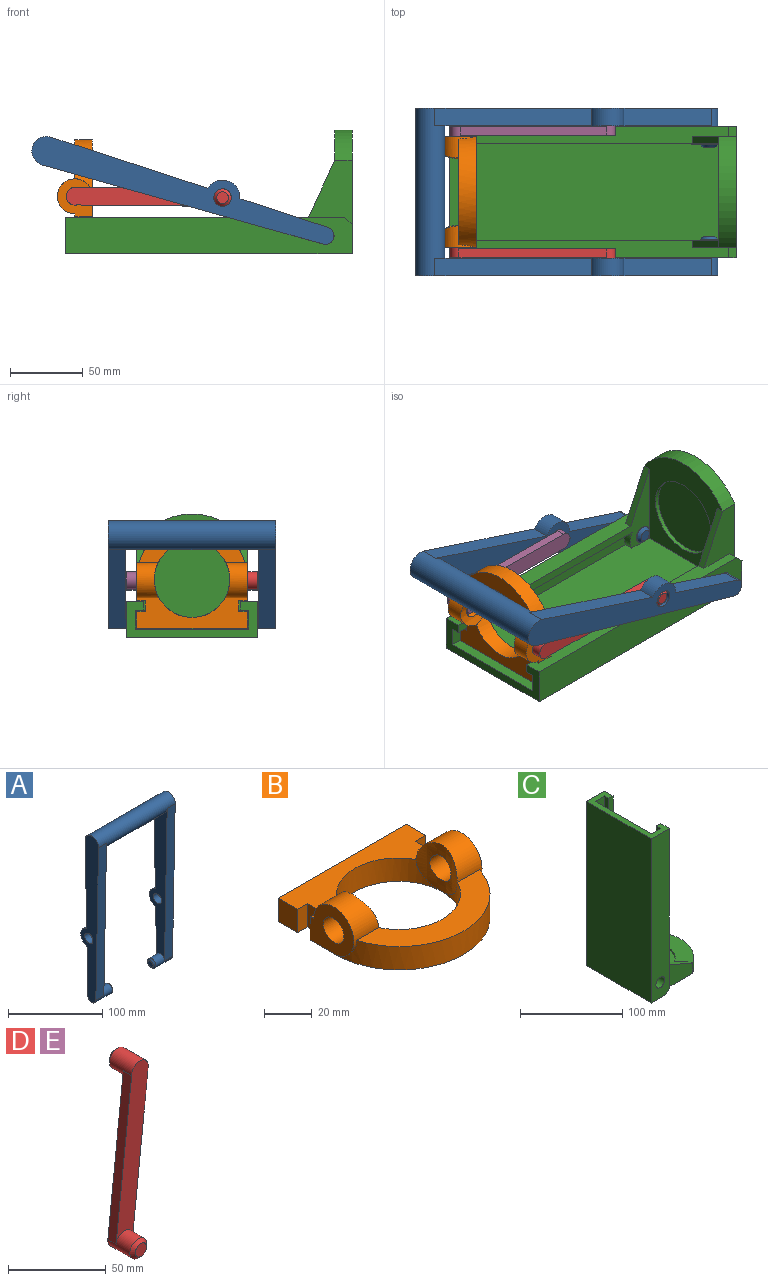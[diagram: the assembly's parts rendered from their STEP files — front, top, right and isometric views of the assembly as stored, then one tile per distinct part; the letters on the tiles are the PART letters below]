
ASSEMBLY  parts=5 mates=9
PART A: 21 faces, bbox 115x26.5x216 mm
  f0: plane 63.32x12mm, normal (0,1,-0.02), area 760mm2, adj f1,f6,f7,f8
  f1: cylinder r=6mm len=25mm, axis (-1,0,0), area 712.5mm2, adj f0,f3,f6,f7,f10
  f2: plane 8x8mm, normal (1,0,0), area 50.3mm2, adj f10
  f3: plane 200.12x12.01mm, normal (0,-1,-0.02), area 2401.9mm2, adj f1,f5,f6,f7
  f4: plane 113.24x12mm, normal (0,1,-0.02), area 1359.2mm2, adj f5,f6,f7,f8
  f5: cylinder r=10mm len=115mm, axis (1,0,0), area 6481.3mm2, adj f3,f4,f6,f7,f14,f15,f16,f17
  f6: plane 216x26.5mm, normal (-1,0,0), area 3451.9mm2, adj f0,f1,f3,f4,f5,f8,f9
  f7: plane 199.8x26.5mm, normal (1,0,0), area 3024.7mm2, adj f0,f1,f3,f4,f5,f8,f9
  f8: cylinder r=12mm len=23.23mm, axis (1,0,0), area 379.7mm2, adj f0,f4,f6,f7
  f9: cylinder r=6.1mm len=12.2mm, axis (-1,0,0), area 459.9mm2, adj f6,f7
  f10: cone r=4mm half-angle=45deg, axis (-1,0,0), area 88.9mm2, adj f1,f2
  f11: plane 63.32x12mm, normal (0,1,-0.02), area 760mm2, adj f12,f16,f17,f18
  f12: cylinder r=6mm len=25mm, axis (1,0,0), area 712.5mm2, adj f11,f14,f16,f17,f20
  f13: plane 8x8mm, normal (-1,0,0), area 50.3mm2, adj f20
  f14: plane 200.12x12.01mm, normal (0,-1,-0.02), area 2401.9mm2, adj f5,f12,f16,f17
  f15: plane 113.24x12mm, normal (0,1,-0.02), area 1359.2mm2, adj f5,f16,f17,f18
  f16: plane 216x26.5mm, normal (1,0,0), area 3451.9mm2, adj f5,f11,f12,f14,f15,f18,f19
  f17: plane 199.8x26.5mm, normal (-1,0,0), area 3024.7mm2, adj f5,f11,f12,f14,f15,f18,f19
  f18: cylinder r=12mm len=23.23mm, axis (-1,0,0), area 379.7mm2, adj f11,f15,f16,f17
  f19: cylinder r=6.1mm len=12.2mm, axis (1,0,0), area 459.9mm2, adj f16,f17
  f20: cone r=4mm half-angle=45deg, axis (1,0,0), area 88.9mm2, adj f12,f13
PART B: 23 faces, bbox 76x72x24 mm
  f0: extruded ~24x24mm, area 347.8mm2, adj f4,f5,f20,f22
  f1: extruded ~24x24mm, area 347.8mm2, adj f2,f4,f5,f21
  f2: cylinder r=12mm len=24mm, axis (-1,0,0), area 521.6mm2, adj f1,f3,f6,f7,f10
  f3: cylinder r=38mm len=76mm, axis (0,0,-1), area 1228.1mm2, adj f2,f7,f9,f10,f19,f20
  f4: cylinder r=26mm len=52mm, axis (0,0,-1), area 760.3mm2, adj f0,f1,f7,f19
  f5: cylinder r=26mm len=51.99mm, axis (0,0,-1), area 734.4mm2, adj f0,f1,f6,f19
  f6: plane 76x21mm, normal (0,0,1), area 1068.2mm2, adj f2,f5,f8,f9,f10,f11,f12,f13
  f7: plane 72.75x27mm, normal (0,0,1), area 960.1mm2, adj f2,f3,f4,f20
  f8: plane 12x6mm, normal (0,1,0), area 72mm2, adj f6,f9,f18,f19
  f9: plane 26x24mm, normal (-1,0,0), area 390.4mm2, adj f3,f6,f8,f19,f20,f22
  f10: plane 26x24mm, normal (1,0,0), area 390.4mm2, adj f2,f3,f6,f11,f19,f21
  f11: plane 12x6mm, normal (0,1,0), area 72mm2, adj f6,f10,f12,f19
  f12: plane 12x7.5mm, normal (1,0,0), area 90mm2, adj f6,f11,f13,f19
  f13: plane 12x6mm, normal (0,-1,0), area 72mm2, adj f6,f12,f14,f19
  f14: plane 12x11.5mm, normal (1,0,0), area 138mm2, adj f6,f13,f15,f19
  f15: plane 76x12mm, normal (0,1,0), area 912mm2, adj f6,f14,f16,f19
  f16: plane 12x11.5mm, normal (-1,0,0), area 138mm2, adj f6,f15,f17,f19
  f17: plane 12x6mm, normal (0,-1,0), area 72mm2, adj f6,f16,f18,f19
  f18: plane 12x7.5mm, normal (-1,0,0), area 90mm2, adj f6,f8,f17,f19
  f19: plane 76x72mm, normal (0,0,-1), area 2638.5mm2, adj f3,f4,f5,f8,f9,f10,f11,f12
  f20: cylinder r=12mm len=24mm, axis (-1,0,0), area 521.6mm2, adj f0,f3,f6,f7,f9
  f21: cylinder r=6.1mm len=12.85mm, axis (-1,0,0), area 474mm2, adj f1,f10
  f22: cylinder r=6.1mm len=12.85mm, axis (-1,0,0), area 474mm2, adj f0,f9
PART C: 28 faces, bbox 85x90x197 mm
  f0: plane 79x76mm, normal (0,0,1), area 2665.9mm2, adj f3,f4,f7,f10,f15,f22,f23,f26
  f1: plane 197x25mm, normal (0,1,0), area 4795.6mm2, adj f5,f6,f16,f17,f20,f24
  f2: plane 197x25mm, normal (0,-1,0), area 4795.6mm2, adj f5,f6,f9,f17,f21,f25
  f3: cylinder r=45mm len=76mm, axis (0,0,-1), area 1086mm2, adj f0,f6,f22,f23
  f4: plane 185x78mm, normal (1,0,0), area 14227.3mm2, adj f0,f10,f12,f13,f15,f17,f18,f19
  f5: plane 197x90mm, normal (-1,0,0), area 17730mm2, adj f1,f2,f6,f17
  f6: plane 90x85mm, normal (0,0,-1), area 6272.1mm2, adj f1,f2,f3,f5,f22,f23,f24,f25
  f7: cylinder r=27mm len=54mm, axis (0,0,1), area 508.9mm2, adj f0,f8
  f8: plane 54x54mm, normal (0,0,1), area 2290.2mm2, adj f7
  f9: plane 192x12mm, normal (1,0,0), area 2179mm2, adj f2,f10,f17,f22,f25,f26
  f10: plane 185x58mm, normal (0,1,0), area 1576.4mm2, adj f0,f4,f9,f11,f17,f19,f21,f26
  f11: plane 168.75x6mm, normal (-1,0,0), area 1012.5mm2, adj f10,f12,f17,f19
  f12: plane 168.75x13mm, normal (0,1,0), area 2172.7mm2, adj f4,f11,f17,f19
  f13: plane 168.75x13mm, normal (0,-1,0), area 2172.7mm2, adj f4,f14,f17,f18
  f14: plane 168.75x6mm, normal (-1,0,0), area 1012.5mm2, adj f13,f15,f17,f18
  f15: plane 185x58mm, normal (0,-1,0), area 1576.4mm2, adj f0,f4,f14,f16,f17,f18,f20,f27
  f16: plane 192x12mm, normal (1,0,0), area 2179mm2, adj f1,f15,f17,f23,f24,f27
  f17: plane 90x25mm, normal (0,0,1), area 840mm2, adj f1,f2,f4,f5,f9,f10,f11,f12
  f18: cylinder r=12mm len=13mm, axis (0,1,0), area 82.5mm2, adj f4,f13,f14,f15
  f19: cylinder r=12mm len=13mm, axis (0,-1,0), area 82.5mm2, adj f4,f10,f11,f12
  f20: cylinder r=6.1mm len=12.2mm, axis (0,1,0), area 459.9mm2, adj f1,f15
  f21: cylinder r=6.1mm len=12.2mm, axis (0,1,0), area 459.9mm2, adj f2,f10
  f22: plane 44.1x30mm, normal (0,-1,0), area 832.7mm2, adj f0,f3,f6,f9,f25,f26
  f23: plane 44.1x30mm, normal (0,1,0), area 832.7mm2, adj f0,f3,f6,f16,f24,f27
  f24: plane 7x5mm, normal (0.71,0,-0.71), area 49.5mm2, adj f1,f6,f16,f23
  f25: plane 7x5mm, normal (0.71,0,-0.71), area 49.5mm2, adj f2,f6,f9,f22
  f26: plane 39x18mm, normal (0.42,0,0.91), area 214.8mm2, adj f0,f9,f10,f22
  f27: plane 39x18mm, normal (0.42,0,0.91), area 214.8mm2, adj f0,f15,f16,f23
PART D: 10 faces, bbox 23.3x30x112.7 mm
  f0: cylinder r=6mm len=16mm, axis (0,1,0), area 490.1mm2, adj f2,f5,f6,f7,f8
  f1: plane 8x8mm, normal (0,-1,0), area 50.3mm2, adj f8
  f2: plane 107.4x23.23mm, normal (0,-1,0), area 1212.9mm2, adj f0,f3,f6,f7
  f3: cylinder r=6mm len=16mm, axis (0,-1,0), area 495.6mm2, adj f2,f5,f6,f7,f9
  f4: plane 8x8mm, normal (0,1,0), area 50.3mm2, adj f9
  f5: plane 106.49x23.23mm, normal (0,1,0), area 1212.9mm2, adj f0,f3,f6,f7
  f6: plane 99.82x11.24mm, normal (-0.99,0,0.11), area 602.7mm2, adj f0,f2,f3,f5
  f7: plane 100.74x11.27mm, normal (0.99,0,-0.11), area 608.2mm2, adj f0,f2,f3,f5
  f8: cone r=6mm half-angle=45deg, axis (0,1,0), area 88.9mm2, adj f0,f1
  f9: cone r=4mm half-angle=45deg, axis (0,-1,0), area 88.9mm2, adj f3,f4
PART E: same geometry as D
PLACE A rot(axis=(0.51,-0.51,-0.69),110.8deg) t=(113.73,15.21,-11.47)mm
PLACE B rot(axis=(-0.58,-0.58,0.58),120deg) t=(-46.09,-37.2,12.74)mm
PLACE C rot(axis=(0,-1,0),90deg) t=(132.23,-30.29,21.03)mm
PLACE D rot(axis=(0,-1,0),95.9deg) t=(133.16,15.71,32.7)mm
PLACE E rot(axis=(-0.66,0,0.75),180deg) t=(132.82,-76.29,-5.02)mm
MATE slider C.f7 <-> B.f4  axis (-1,0,0) through (120.23,-30.29,16.03)mm
MATE parallel D.f5 <-> B.f9  axis (0,1,0) through (-2.64,-69.29,15.06)mm
MATE cylindrical A.f8 <-> D.f0  axis (0,-1,0) through (43.27,-87.79,14.63)mm
MATE cylindrical B.f4 <-> C.f7  axis (1,0,0) through (-58.09,-30.29,16.03)mm
MATE cylindrical A.f1 <-> C.f20  axis (0,1,0) through (113.73,-60.79,-11.47)mm
MATE cylindrical E.f0 <-> A.f8  axis (0,1,0) through (43.27,26.71,14.63)mm
MATE cylindrical D.f3 <-> B.f2  axis (0,1,0) through (-58.09,-57.29,15.53)mm
MATE cylindrical B.f2 <-> E.f9  axis (0,-1,0) through (-58.09,-5.22,15.53)mm
MATE parallel E.f5 <-> B.f10  axis (0,-1,0) through (-2.64,8.71,15.02)mm
